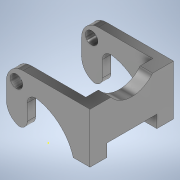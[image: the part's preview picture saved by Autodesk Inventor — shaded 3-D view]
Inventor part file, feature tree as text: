
AUTODESK INVENTOR PART (.ipt)
format: ipt  version: 2021 (Build 250183000, 183)  size: 199,680 bytes
history: native  units: mm
features: sketch x7, extrude x6, fillet x3, other x1
ambient origin geometry x8: Origin, YZ Plane, XZ Plane, XY Plane, X Axis, Y Axis, Z Axis, Center Point
bodies: Body1 (feature_tree)
feature tree (17):
  other  "Sólido1"
  extrude  "Extrusão1"  Depth=10.0mm
  extrude  "Extrusão2"  Depth=2.0mm
  extrude  "Extrusão3"  Depth=2.0mm
  sketch  "Esboço4"  dims[d11=2.5mm d12=5.504926mm]
  fillet  "Arredondamento1"  Radius=1.5mm
  fillet  "Arredondamento2"  Radius=6.0mm
  fillet  "Arredondamento3"  Radius=2.0mm
  extrude  "Extrusão4"  Depth=5.504926mm
  extrude  "Extrusão5"  TaperAngle=0.0deg  [1 undecoded]
  extrude  "Extrusão6"  Depth=1.0mm
  sketch  "Esboço1"  dims[d0=10.0mm d1=10.0mm]
  sketch  "Esboço2"  dims[d2=6.0mm d3=0.0mm d4=2.0mm]
  sketch  "Esboço3"  dims[d5=1.5mm d6=2.0mm d7=1.5mm d8=6.0mm d9=0.0mm d10=2.0mm]
  sketch  "Esboço5"  dims[d13=2.708687mm d14=0.0mm d15=0.0mm]
  sketch  "Esboço6"  dims[d16=1.0mm d17=1.0mm]
  sketch  "Esboço7"  dims[d18=2.0mm d19=1.5mm d20=8.8mm d21=4.5mm d22=0.0mm d23=0.0mm d24=1.0mm d25=1.0mm d26=1.5mm d27=0.0mm d28=0.0mm d29=3.2mm d30=2.5mm d31=2.5mm d32=6.0mm d33=0.0mm]
note: 1 required parameter value undecoded (feature->parameter linkage not recoverable at this tier; creation-order binding heuristic only, values carry confidence <= 0.55)
